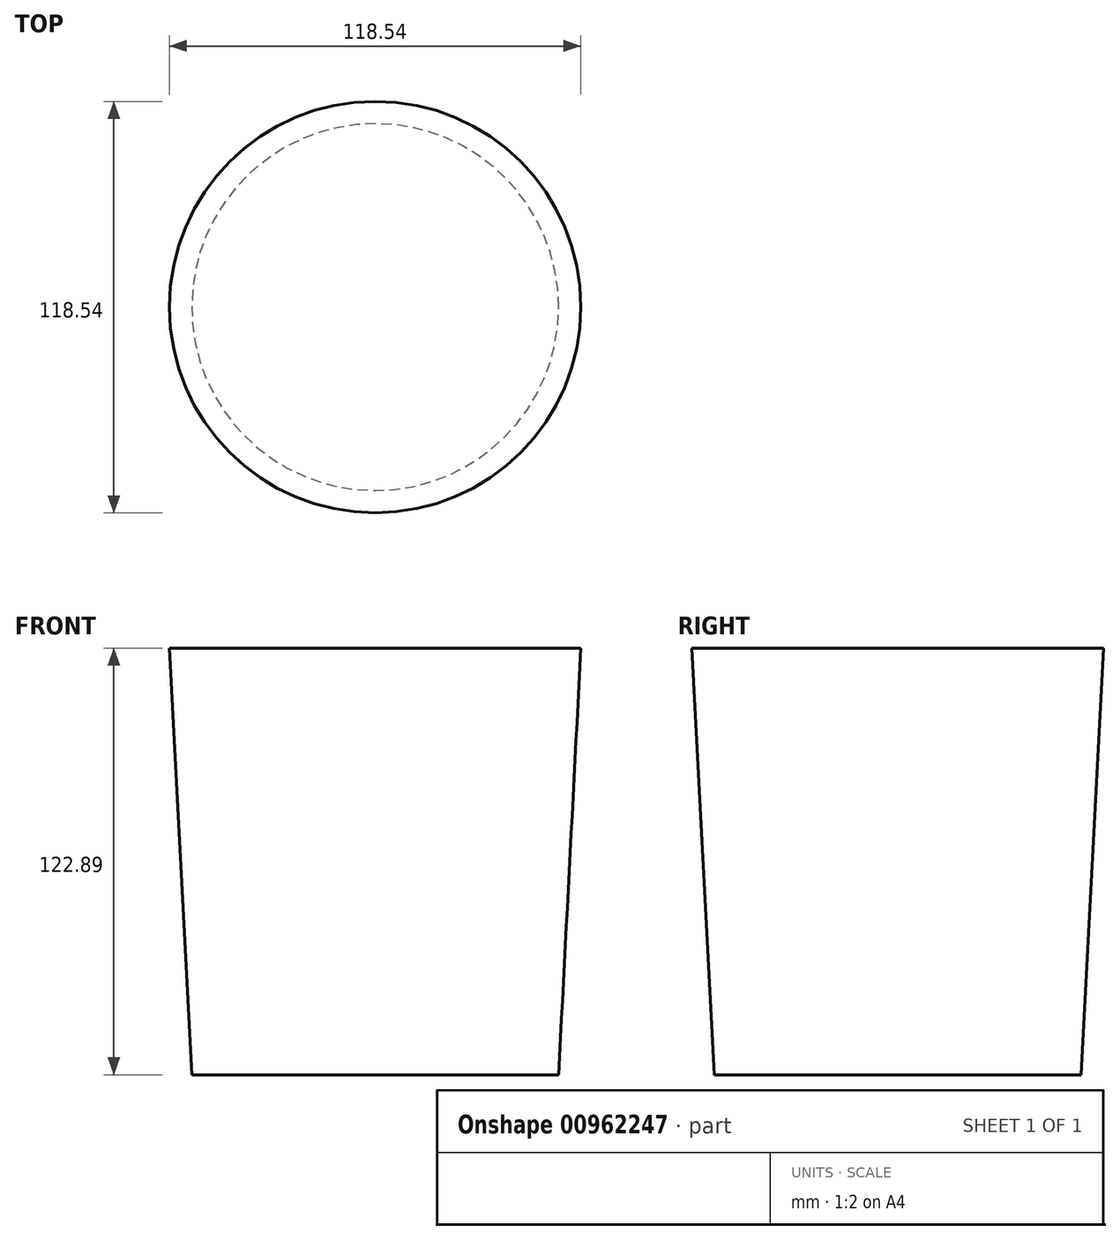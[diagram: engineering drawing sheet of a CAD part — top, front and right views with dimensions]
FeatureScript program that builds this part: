
annotation { "Feature Type Name" : "Feature", "Feature Type Description" : "" }
export const myFeature = defineFeature(function(context is Context, id is Id, definition is map)
    precondition{}
    {
        {
            var Q0;
            Q0=qCreatedBy(makeId("Top.planeOp"),FACE);
            var sketch = newSketch(context, id + "F0", { "sketchPlane" : qUnion([Q0])});
            skCircle(sketch, "E0", {"center": v(0, 0) * mm, "radius": 52.83 * mm});
            skSolve(sketch);
        }
        {
            var Q0;
            Q0=makeQuery(id+"F0.imprint","IMPRINT",FACE,{"disambiguationData":[TD([[makeQuery(id+"F0.imprint","IMPRINT",EDGE,{"derivedFrom":sQuery(id+"F0.wireOp",EDGE,"E0")}),1.0]])]});
            extrude(context, id + "F1", {"entities" : qUnion([Q0]), "depth" : 122.89 * mm, "offsetDistance" : 25.4 * mm, "hasDraft" : true, "draftAngle" : 3 * degree});
        }
    });
